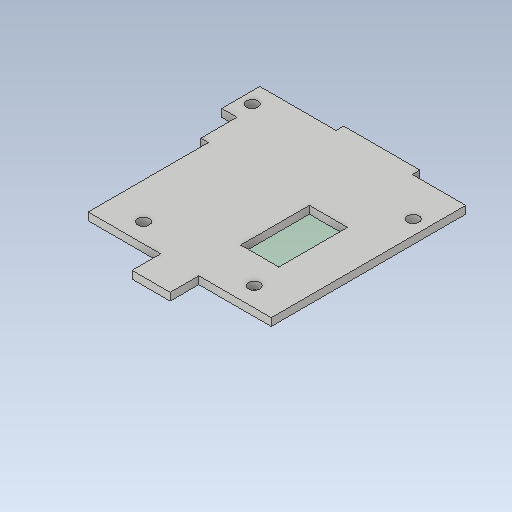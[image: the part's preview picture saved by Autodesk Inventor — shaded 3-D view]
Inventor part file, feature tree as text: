
AUTODESK INVENTOR PART (.ipt)
format: ipt  version: 2020.1 (Build 241239000, 239)  size: 181,248 bytes
history: native  units: mm
features: extrude x7, sketch x7, other x1, plane x1
ambient origin geometry x8: Origin, YZ Plane, XZ Plane, XY Plane, X Axis, Y Axis, Z Axis, Center Point
bodies: Body1 (feature_tree)
feature tree (16):
  other  "Sólido1"
  extrude  "Extrusión1"  Depth=51.0mm
  plane  "Plano de trabajo1"
  extrude  "Extrusión4"  Depth=5.0mm
  extrude  "Extrusión6"  Depth=3.0mm
  extrude  "Extrusión7"  Depth=2.0mm
  extrude  "Extrusión8"  Depth=20.0mm
  extrude  "Extrusión9"  Depth=29.5mm
  extrude  "Extrusión10"  Depth=10.0mm
  sketch  "Boceto1"  dims[d0=48.0mm d1=51.0mm]
  sketch  "Boceto4"  dims[d3=5.0mm d4=5.0mm]
  sketch  "Boceto6"  dims[d5=8.75mm d6=3.0mm]
  sketch  "Boceto7"  dims[d7=2.0mm d8=0.0mm d18=2.0mm]
  sketch  "Boceto8"  dims[d19=10.0mm d20=20.0mm]
  sketch  "Boceto9"  dims[d21=2.0mm d22=0.0mm d26=29.5mm]
  sketch  "Boceto10"  dims[d27=21.0mm d28=10.0mm d29=6.0mm d30=2.0mm d31=0.0mm d32=2.0mm d33=0.0mm d34=19.5mm d35=2.0mm d36=9.5mm d37=4.0mm d38=2.0mm d39=0.0mm d40=5.0mm d41=9.5mm d42=38.5mm d43=3.0mm d44=3.0mm d45=10.0mm d46=3.75mm d47=3.0mm d48=3.0mm d49=3.0mm d50=2.0mm d51=0.0mm d52=2.0mm d53=4.0mm d54=2.0mm d55=4.0mm d56=10.0mm d57=0.0mm]
